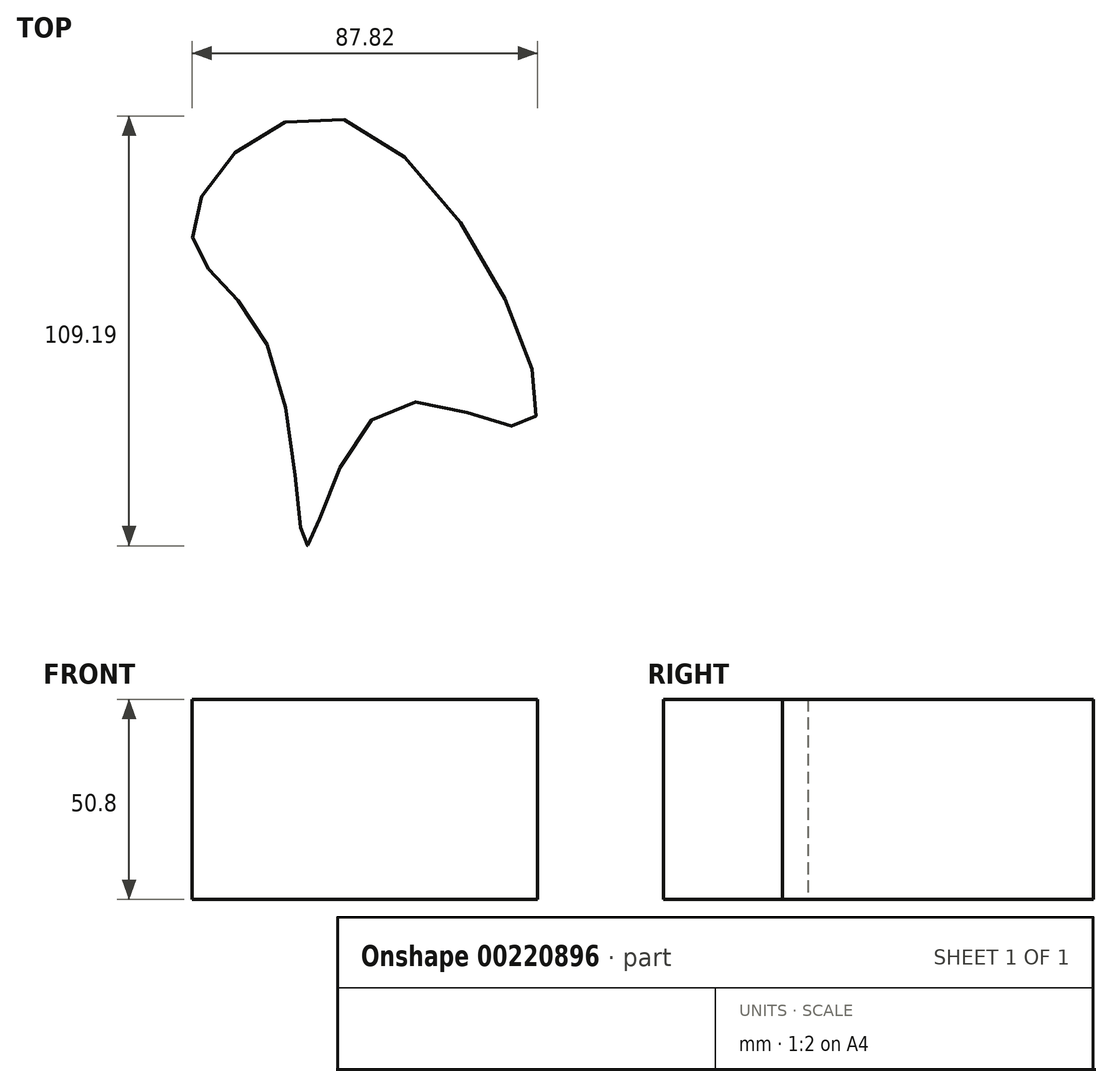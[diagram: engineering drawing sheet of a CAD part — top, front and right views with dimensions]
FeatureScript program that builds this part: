
annotation { "Feature Type Name" : "Feature", "Feature Type Description" : "" }
export const myFeature = defineFeature(function(context is Context, id is Id, definition is map)
    precondition{}
    {
        {
            var Q0;
            Q0=qCreatedBy(makeId("Top.planeOp"),FACE);
            var sketch = newSketch(context, id + "F0", { "sketchPlane" : qUnion([Q0])});
            skFitSpline(sketch, "E0", {"points": [v(-26.58, -8.33) * mm, v(-45.66, 21.14) * mm, v(-6.6, 48.64) * mm, v(40.94, -28) * mm, v(4.8, -24.07) * mm, v(-16.46, -59.48) * mm, v(-26.58, -8.33) * mm]});
            skSolve(sketch);
        }
        {
            var Q0;
            Q0=makeQuery(id+"F0.imprint","IMPRINT",FACE,{"disambiguationData":[TD([[makeQuery(id+"F0.imprint","IMPRINT",EDGE,{"derivedFrom":sQuery(id+"F0.wireOp",EDGE,"E0")}),-1.0]])]});
            extrude(context, id + "F1", {"entities" : qUnion([Q0]), "depth" : 50.8 * mm});
        }
    });
